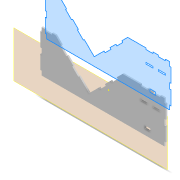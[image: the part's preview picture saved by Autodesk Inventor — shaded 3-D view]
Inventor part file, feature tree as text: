
AUTODESK INVENTOR PART (.ipt)
format: ipt  version: 2022 (Build 260153000, 153)  size: 264,192 bytes
history: native  units: mm
features: sketch x5, reference x5, other x5, extrude x3, projected_geometry x2, plane x1
ambient origin geometry x8: Origin, YZ Plane, XZ Plane, XY Plane, X Axis, Y Axis, Z Axis, Center Point
bodies: Solid1 (feature_tree)
feature tree (21):
  plane  "Work Plane1"
  extrude  "Extrusion1"  Depth=25.0mm
  sketch  "Sketch3"  dims[d17=5.0mm d18=100.0mm]
  extrude  "Extrusion3"  Depth=100.0mm
  sketch  "Sketch5"  dims[d22=15.0mm]
  extrude  "Extrusion4"  Depth=5.0mm
  sketch  "Sketch1"  dims[d0=5.0mm d1=0.0mm d16=25.0mm]
  reference  "Reference1"
  reference  "Reference2"
  reference  "Reference3"
  reference  "Reference4"
  reference  "Reference5"
  sketch  "Sketch4"  dims[d19=25.0mm d20=5.0mm]
  projected_geometry  "Projected Loop2"
  sketch  "Sketch6"  dims[d23=5.0mm d24=0.0mm d25=20.0mm d26=20.0mm d27=10.0mm d28=20.0mm d29=50.0mm d30=10.0mm d31=0.0mm]
  projected_geometry  "Projected Loop3"
  parser-record x1  (decoder bookkeeping rows leaked as tree rows — omitted from the tree; the rows remain in map.json)
  other  "Ensamble caja.iam"
  other  "Modelo base:1"
  other  "Lateral:1"
  other  "Lateral:2"
note: 1 file-system path scrubbed to <path> (originals preserved in map.json)
